# Revit family: Safety-Railing_Hatch_SafetyRail_HatchGuard
name_source: partatom
category: Generic Models
units: mm (PartAtom-declared; Revit-internal decimal feet)

## family parameters
Always vertical = No
Can host rebar = No
Classification Number = 23.30.80.11
Cut with Voids When Loaded = No
Maintain Annotation Orientation = No
Part Type = Normal
Room Calculation Point = No
Round Connector Dimension = Use Diameter
Shared = No
Work Plane-Based = Yes

## types (5) — shared parameters
Construction Details = http://www.arcat.com
Default Elevation = 0' - 0"
Green Building-LEED = http://www.arcat.com
Keynote = 05 52 17
Manufacturer = Safety Rail Company
Manufacturer Fax = 888-471-4931
Manufacturer Website = http://www.safetyrailcompany.com
Model = Hatch Guard
Product Data = http://www.arcat.com
Product Properties = http://www.safetyrailcompany.com
Revision = R1_2017-08
Sales Information = http://www.safetyrailcompany.com
SpecWizard = http://www.arcat.com
Specification = http://www.arcat.com
Standards Conformance = OSHA
Type Comments = Custom Sizes Available
URL = http://www.safetyrailcompany.com
Unit Height = 3' - 6"
zero-valued in all types: Expected Lifespan (Years), Maintenance Schedule (Months), Warranty Duration (Years)

## per-type parameters (varying)
| type | Description | Opening Depth | Opening Width | Unit Length | Unit Width | gatearmwidth | gatewidth |
| 36 x 100 Opening | Safety Rail Company Hatch Fall Protection - Hatch Guard 36100 as Specified | 8' - 4" | 3' - 0" | 11' - 6 3/16" | 3' - 8" | 3' - 0 5/8" | 3' - 0 5/8" |
| 36 x 58 Opening | Safety Rail Company Hatch Fall Protection - Hatch Guard 3658 as Specified | 4' - 10" | 3' - 0" | 7' - 4 3/16" | 3' - 8" | 3' - 0 5/8" | 3' - 0 5/8" |
| 32 x 46 Opening | Safety Rail Company Hatch Fall Protection - Hatch Guard 3246 as Specified | 3' - 10" | 2' - 8" | 6' - 6 3/16" | 4' - 6" | 2' - 8 5/8" | 2' - 8 5/8" |
| 42 x 36 Opening | Safety Rail Company Hatch Fall Protection - Hatch Guard 4236 as Specified | 3' - 6" | 3' - 0" | 6' - 4 3/16" | 3' - 8" | 3' - 0 5/8" | 3' - 0 5/8" |
| 42 x 42 Opening | Safety Rail Company Hatch Fall Protection - Hatch Guard 4242 as Specified | 3' - 6" | 3' - 6" | 6' - 2 3/16" | 4' - 2" | 3' - 6 5/8" | 3' - 6 5/8" |

## geometry (parser evidence)
native form markers: Sweep x4
no freeform markers — native parametric forms only
